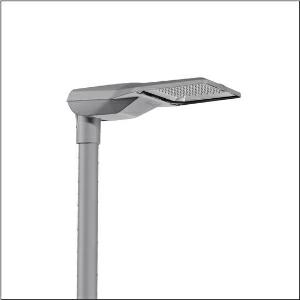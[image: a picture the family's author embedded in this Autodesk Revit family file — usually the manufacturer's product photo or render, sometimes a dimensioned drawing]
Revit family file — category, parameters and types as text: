
# Revit family: streetlight_sl_21_iq_midi___pc-l_5xe3f31g08mb_a45c
name_source: partatom
category: Lighting Fixtures
units: mm (PartAtom-declared; Revit-internal decimal feet)

## family parameters
Cut with Voids When Loaded = No
Host = Face
Light Source = No
Part Type = Normal
Room Calculation Point = No
Round Connector Dimension = Use Diameter
Shared = No

## types (1)
- --- (1 x LED, 18560 lm, 146.7 W, 3000K)
    Apparent Load = 147 VA
    CIE Flux Codes = 38 78 98 100 100
    Color Rendering = 70
    Color Temperature = 3000K
    Default Elevation = 1800 mm
    Description = Streetlight SL 21 iQ midi, mast luminaire, primary light control with lens, of PMMA, primary optical cover: cover, of toughened safety glass, transparent, light distribution: PC-L, light emission: direct distribution, primary light characteristic: asymmetric, left, installation type: post-top, side-entry, LED, High Power LED, rated luminous flux: 18.560lm, luminous efficacy: 127lm/W, light colour: 730, colour temperature: 3000K, control: Street-Remote, Auto-Match, Temp-Guard, Lumen-Switch, Night-Set, Smart-Wire, Light-Fading, Desk-Remote (wireless, voltage-free reading and setting of iQ features in the workshop via application-optimized NFC function/RFID function), optimised constant luminous flux control (CLO 2.0), presetting dimming linear, mains connection: 230..240V, AC, 50/60Hz, start of lifetime: 147W, end of service life: 161W, reduction: 62W, luminaire housing, of diecast aluminium, powder-coated, Siteco® metallic grey (DB 702S), corrosivity category C5 mid according to DIN EN ISO 12944, please order mast flange separately, inclination adjustable: 0°, 5°, 10°, 15°, sealing non-destructively replaceable, multi-level sealing system, length: 644mm, width: 335mm, height: 110mm, mast flange for spigot size: 42mm (side-entry): 5XC10008XM4, 60/48mm (side-entry/post-top): 5XC10108XM2, 76/60mm (side-entry/post-top): 5XC10108XM1, protection rating (complete): IP66, insulation class (complete): insulation class II (safety insulation), certification: CE, ENEC, ENEC+, VDE, impact resistance: IK09, permissible operating ambient temperature for outdoor applications: -40..+50°C, standard-compliant lighting for roads and squares, packaging unit: 1 piece

Light Distribution: PC-L
    Height = 111 mm
    Lamp = 1 x LED
    Lamp Light Flux = 18560 lm
    Lamp Power = 146.7 W
    Lamp count = 1
    Length = 644 mm
    Luminous efficacy = 127 lm/W
    Manufacturer = Siteco
    ModVariant = No
    Model = 5XE3F31G08MB
    Number of Poles = 1
    OnlyDefault = Yes
    Power Factor = 1
    Product Name = Streetlight SL 21 iQ midi | PC-L
    Product group = mast luminaire | pylon top
    ProductGroupID = 6100
    Protection Class = Protection class II
    Protection Degree = IP 66
    RLX_Detail_Level = 1
    RLX_Emergency_Light_Flux = 0 lm
    RLX_Emergency_Type = 0
    RLX_Emergency_Type_DB = No
    RlxData = <blob elided: 92949 chars, md5=2db84f91>
    Socket = socket
    Standby Power = 0 W
    System Light Flux = 18560 lm
    System Power = 147 W
    Type Comments = factory setting: luminous flux: 100 % | dim-lin: 254 | 753 mA
    Type Image = l_1004298.jpg
    URL = http://relux.com
    VarID = @adj_023141
    Voltage = 0 V
    Weight = 0.00 kg
    Width = 336 mm

## geometry (parser evidence)
native form markers: Blend x4, Sweep x11
no freeform markers — native parametric forms only
